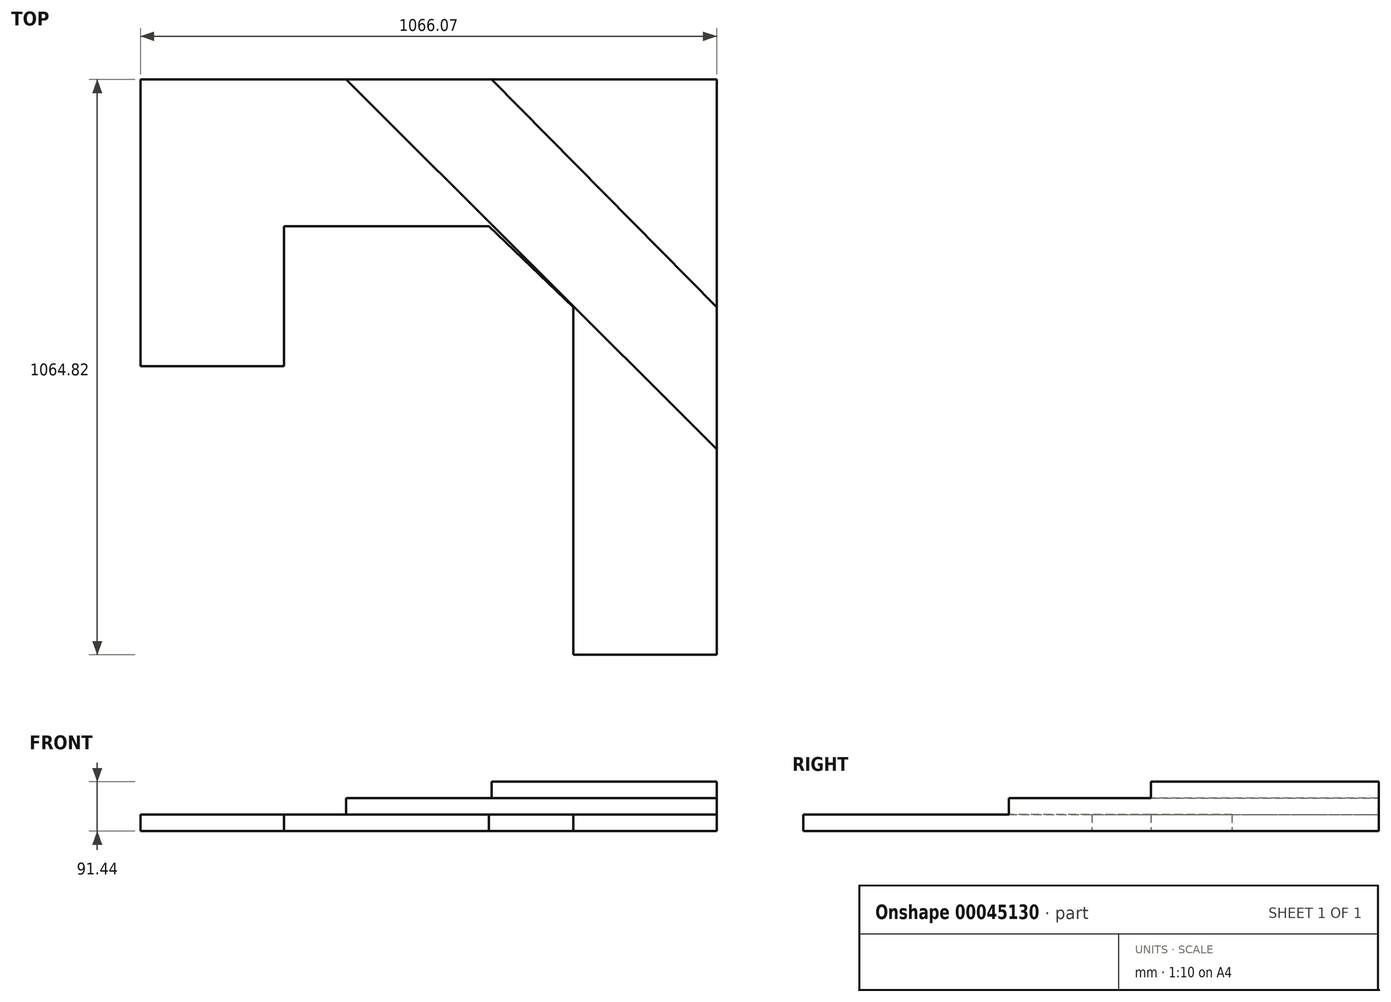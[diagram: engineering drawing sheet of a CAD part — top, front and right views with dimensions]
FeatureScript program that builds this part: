
annotation { "Feature Type Name" : "Feature", "Feature Type Description" : "" }
export const myFeature = defineFeature(function(context is Context, id is Id, definition is map)
    precondition{}
    {
        {
            var Q0;
            Q0=qCreatedBy(makeId("Top.planeOp"),FACE);
            var sketch = newSketch(context, id + "F0", { "sketchPlane" : qUnion([Q0])});
            skLineSegment(sketch, "E0", {"start": v(-1066.07, -530.35) * mm, "end": v(-1066.07, 0) * mm});
            skLineSegment(sketch, "E1", {"start": v(-1066.07, 0) * mm, "end": v(-1066.07, -530.35) * mm});
            skLineSegment(sketch, "E2", {"start": v(-1066.07, -530.35) * mm, "end": v(-800.71, -530.35) * mm});
            skLineSegment(sketch, "E3", {"start": v(-800.71, -530.35) * mm, "end": v(-800.71, -271.25) * mm});
            skLineSegment(sketch, "E4", {"start": v(-800.71, -271.25) * mm, "end": v(-421.45, -271.25) * mm});
            skLineSegment(sketch, "E5", {"start": v(-421.45, -271.25) * mm, "end": v(-264.99, -421.45) * mm});
            skLineSegment(sketch, "E6", {"start": v(-264.99, -421.45) * mm, "end": v(-264.99, -1064.82) * mm});
            skLineSegment(sketch, "E7", {"start": v(-264.99, -1064.82) * mm, "end": v(0, -1064.82) * mm});
            skLineSegment(sketch, "E8", {"start": v(0, -1064.82) * mm, "end": v(0, 0) * mm});
            skLineSegment(sketch, "E9", {"start": v(0, 0) * mm, "end": v(-1066.07, 0) * mm});
            skSolve(sketch);
        }
        {
            var Q0;
            Q0 = qSketchRegion(id + "F0", true);
            extrude(context, id + "F1", {"entities" : qUnion([Q0]), "depth" : 30.48 * mm});
        }
        {
            var Q0;
            Q0=qCreatedBy(makeId("Top.planeOp"),FACE);
            var sketch = newSketch(context, id + "F2", { "sketchPlane" : qUnion([Q0])});
            skLineSegment(sketch, "E10", {"start": v(-685.56, 0) * mm, "end": v(0, -684.3) * mm});
            skLineSegment(sketch, "E11", {"start": v(0, -684.3) * mm, "end": v(0, 0) * mm});
            skLineSegment(sketch, "E12", {"start": v(0, 0) * mm, "end": v(-685.56, 0) * mm});
            skSolve(sketch);
        }
        {
            var Q0;
            Q0 = qSketchRegion(id + "F2", true);
            extrude(context, id + "F3", {"entities" : qUnion([Q0]), "operationType" : NewBodyOperationType.ADD, "depth" : 60.96 * mm});
        }
        {
            var Q0;
            Q0=qCreatedBy(makeId("Top.planeOp"),FACE);
            var sketch = newSketch(context, id + "F4", { "sketchPlane" : qUnion([Q0])});
            skLineSegment(sketch, "E13", {"start": v(-416.44, 0) * mm, "end": v(0, -421.45) * mm});
            skLineSegment(sketch, "E14", {"start": v(0, -421.45) * mm, "end": v(0, 0) * mm});
            skLineSegment(sketch, "E15", {"start": v(0, 0) * mm, "end": v(-416.44, 0) * mm});
            skSolve(sketch);
        }
        {
            var Q0;
            Q0 = qSketchRegion(id + "F4", true);
            extrude(context, id + "F5", {"entities" : qUnion([Q0]), "operationType" : NewBodyOperationType.ADD, "depth" : 91.44 * mm});
        }
    });
